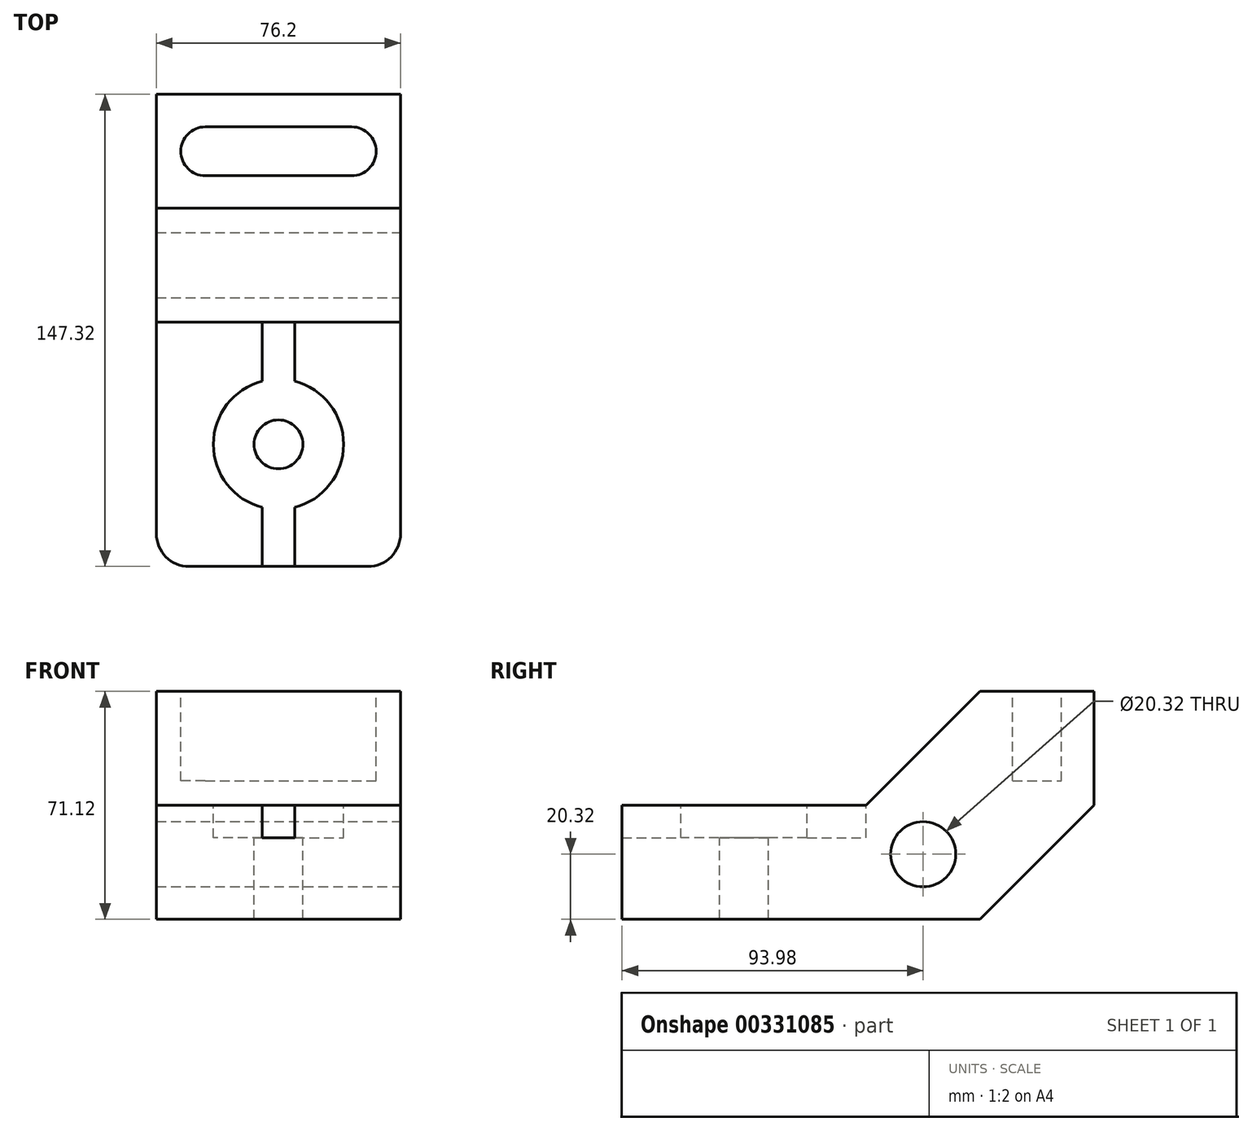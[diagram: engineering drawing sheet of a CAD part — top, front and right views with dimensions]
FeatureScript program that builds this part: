
annotation { "Feature Type Name" : "Feature", "Feature Type Description" : "" }
export const myFeature = defineFeature(function(context is Context, id is Id, definition is map)
    precondition{}
    {
        {
            var Q0;
            Q0=qCreatedBy(makeId("Right.planeOp"),FACE);
            var sketch = newSketch(context, id + "F0", { "sketchPlane" : qUnion([Q0])});
            skLineSegment(sketch, "E0", {"start": v(0, 0) * mm, "end": v(111.76, 0) * mm});
            skLineSegment(sketch, "E1", {"start": v(111.76, 0) * mm, "end": v(147.32, 35.56) * mm});
            skLineSegment(sketch, "E2", {"start": v(147.32, 35.56) * mm, "end": v(147.32, 71.12) * mm});
            skLineSegment(sketch, "E3", {"start": v(147.32, 71.12) * mm, "end": v(111.76, 71.12) * mm});
            skLineSegment(sketch, "E4", {"start": v(111.76, 71.12) * mm, "end": v(76.2, 35.56) * mm});
            skLineSegment(sketch, "E5", {"start": v(76.2, 35.56) * mm, "end": v(0, 35.56) * mm});
            skLineSegment(sketch, "E6", {"start": v(0, 35.56) * mm, "end": v(0, 0) * mm});
            skSolve(sketch);
        }
        {
            var Q0;
            Q0 = qSketchRegion(id + "F0", true);
            extrude(context, id + "F1", {"entities" : qUnion([Q0]), "depth" : 76.2 * mm});
        }
        {
            var Q0;
            Q0=makeQuery(id+"F1.opExtrude","CAP_EDGE",EDGE,{"disambiguationData":[OSD([sQuery(id+"F0.wireOp",EDGE,"E6")])],"isStart":false});
            var Q1;
            Q1=makeQuery(id+"F1.opExtrude","CAP_EDGE",EDGE,{"disambiguationData":[OSD([sQuery(id+"F0.wireOp",EDGE,"E6")])],"isStart":true});
            fillet(context, id + "F2", {"entities" : qUnion([Q0, Q1]), "radius" : 10.16 * mm, "tangentPropagation" : true, "allowEdgeOverflow" : false});
        }
        {
            var Q0;
            Q0=makeQuery(id+"F1.opExtrude","CAP_FACE",FACE,{"disambiguationData":[OSD([sQuery(id+"F0.wireOp",EDGE,"E0"),sQuery(id+"F0.wireOp",EDGE,"E1"),sQuery(id+"F0.wireOp",EDGE,"E2"),sQuery(id+"F0.wireOp",EDGE,"E3"),sQuery(id+"F0.wireOp",EDGE,"E4"),sQuery(id+"F0.wireOp",EDGE,"E5"),sQuery(id+"F0.wireOp",EDGE,"E6")])],"isStart":false});
            var sketch = newSketch(context, id + "F3", { "sketchPlane" : qUnion([Q0])});
            skCircle(sketch, "E7", {"center": v(93.98, 20.32) * mm, "radius": 10.16 * mm});
            skSolve(sketch);
        }
        {
            var Q0;
            Q0 = qSketchRegion(id + "F3", true);
            extrude(context, id + "F4", {"entities" : qUnion([Q0]), "operationType" : NewBodyOperationType.REMOVE, "endBound" : BoundingType.THROUGH_ALL, "oppositeDirection" : true, "depth" : 25.4 * mm});
        }
        {
            var Q0;
            Q0=makeQuery(id+"F1.opExtrude","SWEPT_FACE",FACE,{"disambiguationData":[OSD([sQuery(id+"F0.wireOp",EDGE,"E5")])]});
            var sketch = newSketch(context, id + "F5", { "sketchPlane" : qUnion([Q0])});
            skLineSegment(sketch, "E8.bottom", {"start": v(38.1, 0) * mm, "end": v(43.18, 0) * mm});
            skLineSegment(sketch, "E8.top", {"start": v(38.1, 76.2) * mm, "end": v(43.18, 76.2) * mm});
            skLineSegment(sketch, "E8.left", {"start": v(38.1, 0) * mm, "end": v(38.1, 76.2) * mm});
            skLineSegment(sketch, "E8.right", {"start": v(43.18, 0) * mm, "end": v(43.18, 76.2) * mm});
            skLineSegment(sketch, "E9.bottom", {"start": v(38.1, 0) * mm, "end": v(33.02, 0) * mm});
            skLineSegment(sketch, "E9.top", {"start": v(38.1, 76.2) * mm, "end": v(33.02, 76.2) * mm});
            skLineSegment(sketch, "E9.right", {"start": v(33.02, 0) * mm, "end": v(33.02, 76.2) * mm});
            skCircle(sketch, "E10", {"center": v(38.1, 38.1) * mm, "radius": 12.77 * mm});
            skSolve(sketch);
        }
        {
            var Q0;
            Q0=sQuery(id+"F5.wireOp",VERTEX,"E10.center");
            var Q1;
            Q1=makeQuery(id+"F1.opExtrude","SWEPT_BODY",BODY,{"disambiguationData":[OSD([sQuery(id+"F0.wireOp",EDGE,"E0"),sQuery(id+"F0.wireOp",EDGE,"E1"),sQuery(id+"F0.wireOp",EDGE,"E2"),sQuery(id+"F0.wireOp",EDGE,"E3"),sQuery(id+"F0.wireOp",EDGE,"E4"),sQuery(id+"F0.wireOp",EDGE,"E5"),sQuery(id+"F0.wireOp",EDGE,"E6")])]});
            hole(context, id + "F6", {"style" : HoleStyle.C_BORE, "endStyle" : HoleEndStyle.THROUGH, "holeDiameter" : 15.24 * mm, "cBoreDiameter" : 40.64 * mm, "cBoreDepth" : 10.16 * mm, "tappedDepth" : 12.7 * mm, "tapClearance" : 3, "locations" : qUnion([Q0]), "scope" : qUnion([Q1])});
        }
        {
            var Q0;
            {var subQ0=sQuery(id+"F5.wireOp",EDGE,"E8.bottom");Q0=makeQuery(id+"F5.imprint","IMPRINT",FACE,{"disambiguationData":[TD([[makeQuery(id+"F5.imprint","IMPRINT",EDGE,{"derivedFrom":subQ0}),-1.0]])]});}
            var Q1;
            {var subQ0=sQuery(id+"F5.wireOp",EDGE,"E9.bottom");Q1=makeQuery(id+"F5.imprint","IMPRINT",FACE,{"disambiguationData":[TD([[makeQuery(id+"F5.imprint","IMPRINT",EDGE,{"derivedFrom":subQ0}),-1.0]])]});}
            var Q2;
            {var subQ0=sQuery(id+"F5.wireOp",EDGE,"E8.top");Q2=makeQuery(id+"F5.imprint","IMPRINT",FACE,{"disambiguationData":[TD([[makeQuery(id+"F5.imprint","IMPRINT",EDGE,{"derivedFrom":subQ0}),1.0]])]});}
            var Q3;
            {var subQ0=sQuery(id+"F5.wireOp",EDGE,"E9.top");Q3=makeQuery(id+"F5.imprint","IMPRINT",FACE,{"disambiguationData":[TD([[makeQuery(id+"F5.imprint","IMPRINT",EDGE,{"derivedFrom":subQ0}),1.0]])]});}
            extrude(context, id + "F7", {"entities" : qUnion([Q0, Q1, Q2, Q3]), "operationType" : NewBodyOperationType.REMOVE, "oppositeDirection" : true, "depth" : 10.16 * mm});
        }
        {
            var Q0;
            Q0=makeQuery(id+"F1.opExtrude","SWEPT_FACE",FACE,{"disambiguationData":[OSD([sQuery(id+"F0.wireOp",EDGE,"E3")])]});
            var sketch = newSketch(context, id + "F8", { "sketchPlane" : qUnion([Q0])});
            skLineSegment(sketch, "E11.bottom", {"start": v(15.24, 137.16) * mm, "end": v(60.96, 137.16) * mm});
            skLineSegment(sketch, "E11.top", {"start": v(15.24, 121.92) * mm, "end": v(60.96, 121.92) * mm});
            skLineSegment(sketch, "E11.left", {"start": v(15.24, 137.16) * mm, "end": v(15.24, 121.92) * mm});
            skLineSegment(sketch, "E11.right", {"start": v(60.96, 137.16) * mm, "end": v(60.96, 121.92) * mm});
            skArc(sketch, "E12", {"start": v(60.96, 137.16) * mm, "mid": v(68.58, 129.54) * mm, "end": v(60.96, 121.92) * mm});
            skArc(sketch, "E13", {"start": v(15.24, 137.16) * mm, "mid": v(7.62, 129.54) * mm, "end": v(15.24, 121.92) * mm});
            skSolve(sketch);
        }
        {
            var Q0;
            Q0=makeQuery(id+"F8.imprint","IMPRINT",FACE,{"disambiguationData":[TD([[makeQuery(id+"F8.imprint","IMPRINT",EDGE,{"derivedFrom":sQuery(id+"F8.wireOp",EDGE,"E11.bottom")}),-1.0]])]});
            var Q1;
            Q1=makeQuery(id+"F8.imprint","IMPRINT",FACE,{"disambiguationData":[TD([[makeQuery(id+"F8.imprint","IMPRINT",EDGE,{"derivedFrom":sQuery(id+"F8.wireOp",EDGE,"E11.left")}),-1.0]])]});
            var Q2;
            Q2=makeQuery(id+"F8.imprint","IMPRINT",FACE,{"disambiguationData":[TD([[makeQuery(id+"F8.imprint","IMPRINT",EDGE,{"derivedFrom":sQuery(id+"F8.wireOp",EDGE,"E11.right")}),1.0]])]});
            extrude(context, id + "F9", {"entities" : qUnion([Q0, Q1, Q2]), "operationType" : NewBodyOperationType.REMOVE, "oppositeDirection" : true, "depth" : 27.94 * mm});
        }
    });
